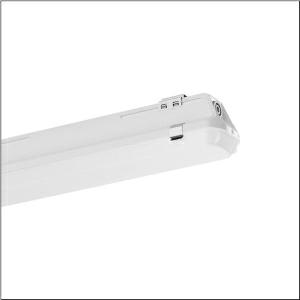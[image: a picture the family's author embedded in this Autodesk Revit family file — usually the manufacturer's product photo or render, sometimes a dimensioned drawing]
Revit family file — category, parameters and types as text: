
# Revit family: monsun_r__11_emergency_51fp10dp460hr_ed92
name_source: partatom
category: Lighting Fixtures
units: mm (PartAtom-declared; Revit-internal decimal feet)

## family parameters
Cut with Voids When Loaded = No
Host = Face
Light Source = No
Part Type = Normal
Room Calculation Point = No
Round Connector Dimension = Use Diameter
Shared = No

## types (1)
- --- (1 x LED, 890 lm, 6.9 W, 4000K)
    Apparent Load = 7 VA
    CIE Flux Codes = 47 77 93 94 100
    Color Rendering = 80
    Color Temperature = 4000K
    Default Elevation = 1800 mm
    Description = Monsun® 11 emergency, damp-proof luminaire, chain hanger, primary optical cover: enclosure, of PMMA, light emission: direct distribution, primary light characteristic: symmetric, installation type: suspended mounting, surface-mounted, horizontal mounting, vertical mounting, LED, rated luminous flux: 6.050lm, luminous efficacy: 175lm/W, light colour: 840, colour temperature: 4000K, control gear: ECG DALI, with terminal, 5+2-pole, max. 2.5mm², mains connection: 220..240V, AC/DC, 0/50..60Hz, rated input power: 35W, changeover relay for equivalent power supply, AC/DC, 0/50..60Hz, luminaire housing, of glass-fibre reinforced polyester, uncoated, bright grey, incl. chain hanger, length: 1.590mm, width: 90mm, height: 88mm, clip for enclosure, of stainless steel (V2A), ceiling mounting element, of stainless steel (V2A), chain hanger, of stainless steel (V2A), protection rating (complete): IP66, insulation class (complete): insulation class I (protective earthing), certification: CE, UKCA, protection symbol: D, impact resistance: IK04, permissible operating ambient temperature: -25..+35°C, standard: EN 50419, EN 60598-2-1, EN 60598-2-22, no direct snow, no direct sun, no direct rain, for indoor or canopied outdoor use, corresponds to IFS (International Featured Standards) requirements for safety and quality in the food industry, contact your sales advisor before using the luminaires in applications with unclear chemical exposure, large temperature fluctuations or condensation-forming humidity, LABS conformity tested according to VDMA 24364:2018-05, packaging unit: 1 piece
    Height = 89 mm
    Lamp = 1 x LED
    Lamp Light Flux = 890 lm
    Lamp Power = 6.9 W
    Lamp count = 1
    Length = 1590 mm
    Luminous efficacy = 129 lm/W
    Manufacturer = Siteco
    ModVariant = No
    Model = 51FP10DP460HR
    Mounting Place = Ceiling
    Mounting Type = Surface mounted
    Number of Poles = 1
    OnlyDefault = Yes
    Power Factor = 1
    Product Name = Monsun® 11 emergency
    Product group = damp-proof luminaire
    ProductGroupID = 301
    Protection Class = Protection class I
    Protection Degree = IP 66
    RLX_Detail_Level = 1
    RLX_Emergency_Light_Flux = 0 lm
    RLX_Emergency_Type = 0
    RLX_Emergency_Type_DB = No
    RlxData = <blob elided: 92301 chars, md5=1cb1d4a2>
    Socket = socket
    Standby Power = 0 W
    System Light Flux = 890 lm
    System Power = 7 W
    Type Comments = : equivalent power supply (DC)
    Type Image = l_1004748.jpg
    URL = http://relux.com
    VarID = @adj_152533
    Voltage = 0 V
    Weight = 0.00 kg
    Width = 90 mm

## geometry (parser evidence)
native form markers: Blend x4, Sweep x12
no freeform markers — native parametric forms only
